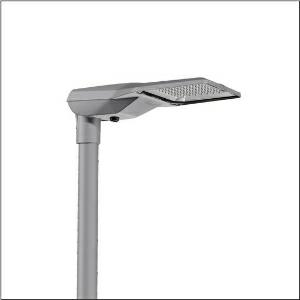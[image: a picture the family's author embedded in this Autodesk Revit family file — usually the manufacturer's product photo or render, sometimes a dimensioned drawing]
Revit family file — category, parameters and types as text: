
# Revit family: streetlight_sl_21_iq_midi___p0_8ab_5xe3r31u08nb_f32c
name_source: partatom
category: Lighting Fixtures
units: mm (PartAtom-declared; Revit-internal decimal feet)

## family parameters
Cut with Voids When Loaded = No
Host = Face
Light Source = No
Part Type = Normal
Room Calculation Point = No
Round Connector Dimension = Use Diameter
Shared = No

## types (1)
- --- (1 x LED, 18710 lm, 136.6 W, 3000K)
    Apparent Load = 137 VA
    CIE Flux Codes = 39 72 97 100 100
    Color Rendering = 70
    Color Temperature = 3000K
    Default Elevation = 1800 mm
    Description = Streetlight SL 21 iQ midi, mast luminaire, primary light control with lens, of PMMA, primary optical cover: cover, of toughened safety glass, transparent, light distribution: P0.8aB, light emission: direct distribution, primary light characteristic: asymmetric, installation type: post-top, side-entry, LED, High Power LED, rated luminous flux: 18.710lm, luminous efficacy: 137lm/W, light colour: 730, colour temperature: 3000K, control gear: iQ-Street Remote, D4i with power reduction, control: pre-setting: logarithmic dimming characteristic, Street-Remote, Auto-Match, Temp-Guard, Lumen-Switch, Night-Set, Smart-Wire, Light-Fading, Desk-Remote (wireless, voltage-free reading and setting of iQ features in the workshop via application-optimized NFC function/RFID function), optimised constant luminous flux control (CLO 2.0), mains connection: 230..240V, AC, 50/60Hz, start of lifetime: 137W, end of service life: 144W, reduction: 61W, luminaire housing, of diecast aluminium, powder-coated, Siteco® metallic grey (DB 702S), corrosivity category C5 mid according to DIN EN ISO 12944, please order mast flange separately, inclination adjustable: 0°, 5°, 10°, 15°, sealing non-destructively replaceable, multi-level sealing system, length: 644mm, width: 335mm, height: 110mm, mast flange for spigot size: 42mm (side-entry): 5XC10008XM4, 60/48mm (side-entry/post-top): 5XC10108XM2, 76/60mm (side-entry/post-top): 5XC10108XM1, mounting height: 4..8m, Smart Interface below, protection rating (complete): IP66, insulation class (complete): insulation class II (safety insulation), certification: CE, ENEC, ENEC+, VDE, impact resistance: IK10, permissible operating ambient temperature for outdoor applications: -40..+50°C, standard-compliant lighting for roads and squares, packaging unit: 1 piece

Light Distribution: P0.8aB
    Height = 111 mm
    Lamp = 1 x LED
    Lamp Light Flux = 18710 lm
    Lamp Power = 136.6 W
    Lamp count = 1
    Length = 644 mm
    Luminous efficacy = 137 lm/W
    Manufacturer = Siteco
    ModVariant = No
    Model = 5XE3R31U08NB
    Number of Poles = 1
    OnlyDefault = Yes
    Power Factor = 1
    Product Name = Streetlight SL 21 iQ midi | P0.8aB
    Product group = mast luminaire | pylon top
    ProductGroupID = 6100
    Protection Class = Protection class II
    Protection Degree = IP 66
    RLX_Detail_Level = 1
    RLX_Emergency_Light_Flux = 0 lm
    RLX_Emergency_Type = 0
    RLX_Emergency_Type_DB = No
    RlxData = <blob elided: 26941 chars, md5=0706ce8b>
    Socket = socket
    Standby Power = 0 W
    System Light Flux = 18710 lm
    System Power = 137 W
    Type Comments = factory setting: luminous flux: 100 % | dim-lin: 254 | 733 mA
    Type Image = l_1004300.jpg
    URL = http://relux.com
    VarID = @adj_071250
    Voltage = 0 V
    Weight = 0.00 kg
    Width = 336 mm

## geometry (parser evidence)
native form markers: Blend x4, Sweep x12
no freeform markers — native parametric forms only
